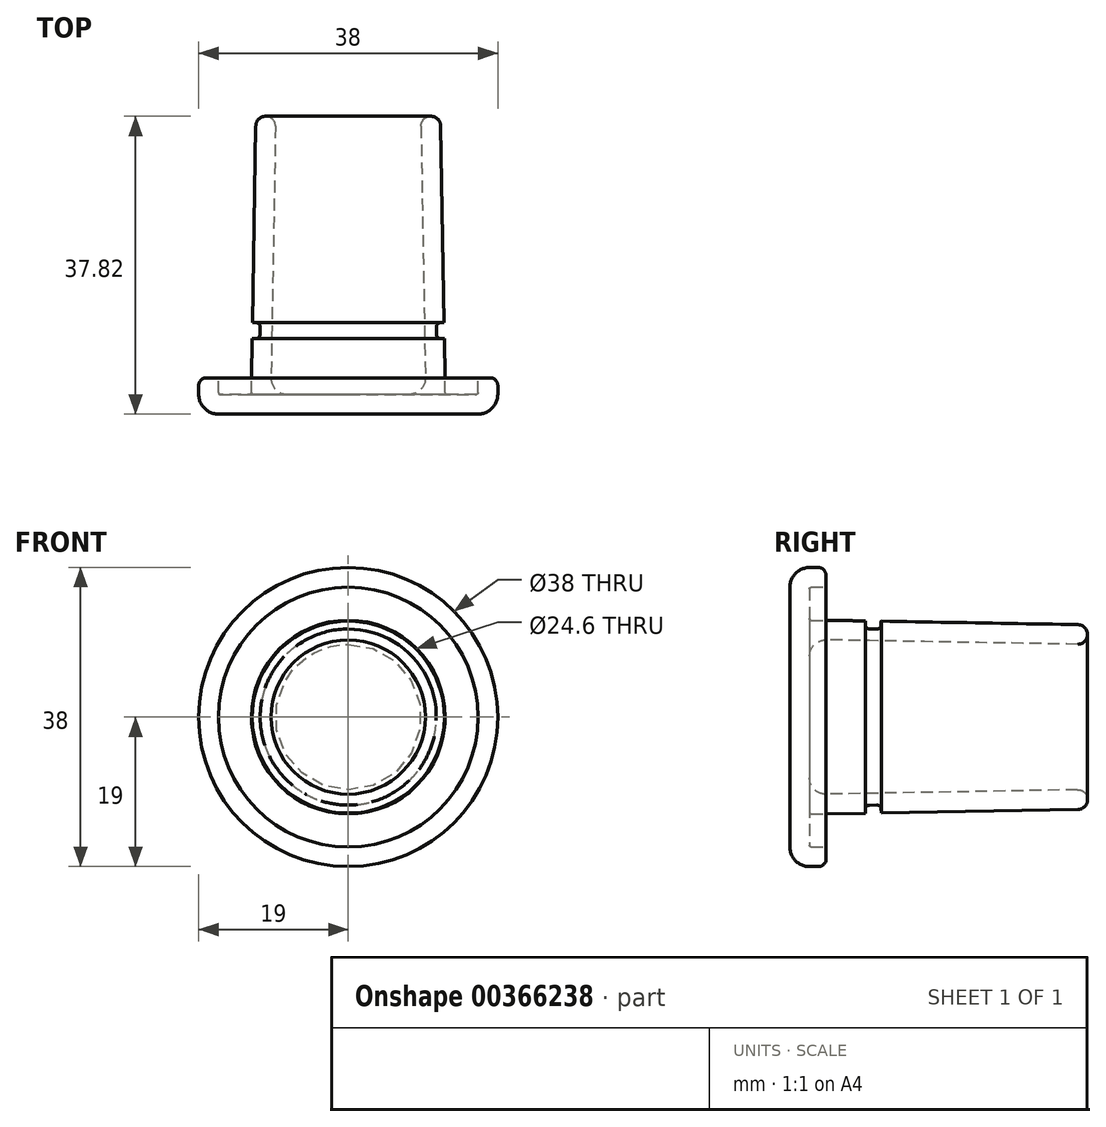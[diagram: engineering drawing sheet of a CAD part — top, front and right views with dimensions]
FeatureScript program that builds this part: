
annotation { "Feature Type Name" : "Feature", "Feature Type Description" : "" }
export const myFeature = defineFeature(function(context is Context, id is Id, definition is map)
    precondition{}
    {
        {
            var Q0;
            Q0=qCreatedBy(makeId("Right.planeOp"),FACE);
            var sketch = newSketch(context, id + "F0", { "sketchPlane" : qUnion([Q0])});
            skLineSegment(sketch, "E0", {"start": v(0, 0) * mm, "end": v(0, 16.5) * mm});
            skLineSegment(sketch, "E1", {"start": v(2.5, 19) * mm, "end": v(3.6, 19) * mm});
            skLineSegment(sketch, "E2", {"start": v(4.6, 18) * mm, "end": v(4.6, 16.7) * mm});
            skLineSegment(sketch, "E3", {"start": v(4.4, 16.5) * mm, "end": v(2.7, 16.5) * mm});
            skLineSegment(sketch, "E4", {"start": v(2.5, 16.3) * mm, "end": v(2.5, 12.5) * mm});
            skLineSegment(sketch, "E5", {"start": v(2.7, 12.3) * mm, "end": v(4.58, 12.3) * mm});
            skLineSegment(sketch, "E6", {"start": v(0, 0) * mm, "end": v(2.5, 0) * mm});
            skArc(sketch, "E7.filletArc", {"start": v(2.5, 19) * mm, "mid": v(0.73, 18.27) * mm, "end": v(0, 16.5) * mm});
            skArc(sketch, "E8.filletArc", {"start": v(4.6, 18) * mm, "mid": v(4.3, 18.7) * mm, "end": v(3.6, 19) * mm});
            skArc(sketch, "E9.filletArc", {"start": v(2.7, 16.5) * mm, "mid": v(2.56, 16.44) * mm, "end": v(2.5, 16.3) * mm});
            skArc(sketch, "E10.filletArc", {"start": v(2.5, 12.5) * mm, "mid": v(2.56, 12.36) * mm, "end": v(2.7, 12.3) * mm});
            skLineSegment(sketch, "E11", {"start": v(2.5, 0) * mm, "end": v(2.5, 7.74) * mm});
            skLineSegment(sketch, "E12", {"start": v(4.56, 9.8) * mm, "end": v(4.56, 9.8) * mm});
            skArc(sketch, "E13.filletArc", {"start": v(4.56, 9.8) * mm, "mid": v(3.1, 9.2) * mm, "end": v(2.5, 7.74) * mm});
            skLineSegment(sketch, "E14", {"start": v(4.58, 12.3) * mm, "end": v(9.6, 12.21) * mm});
            skLineSegment(sketch, "E15", {"start": v(9.6, 12.21) * mm, "end": v(9.6, 11.71) * mm});
            skLineSegment(sketch, "E16", {"start": v(10.08, 11.2) * mm, "end": v(11.08, 11.19) * mm});
            skLineSegment(sketch, "E17", {"start": v(11.6, 11.68) * mm, "end": v(11.6, 12.18) * mm});
            skLineSegment(sketch, "E18", {"start": v(11.6, 12.18) * mm, "end": v(36.6, 11.74) * mm});
            skLineSegment(sketch, "E19", {"start": v(4.56, 9.8) * mm, "end": v(36.55, 9.24) * mm});
            skLineSegment(sketch, "E20", {"start": v(36.6, 11.74) * mm, "end": v(36.55, 9.24) * mm, "construction": true});
            skArc(sketch, "E21", {"start": v(36.6, 11.74) * mm, "mid": v(37.82, 10.47) * mm, "end": v(36.55, 9.24) * mm});
            skPoint(sketch, "E22.visualSharp", {"position": v(9.58, 11.21) * mm});
            skArc(sketch, "E22.filletArc", {"start": v(9.6, 11.71) * mm, "mid": v(9.73, 11.36) * mm, "end": v(10.08, 11.2) * mm});
            skPoint(sketch, "E23.visualSharp", {"position": v(11.58, 11.18) * mm});
            skArc(sketch, "E23.filletArc", {"start": v(11.08, 11.19) * mm, "mid": v(11.44, 11.33) * mm, "end": v(11.6, 11.68) * mm});
            skPoint(sketch, "E24.visualSharp", {"position": v(4.6, 16.5) * mm});
            skArc(sketch, "E24.filletArc", {"start": v(4.4, 16.5) * mm, "mid": v(4.54, 16.56) * mm, "end": v(4.6, 16.7) * mm});
            skLineSegment(sketch, "E25", {"start": v(4.6, 12.3) * mm, "end": v(4.56, 9.8) * mm, "construction": true});
            skLineSegment(sketch, "E26", {"start": v(0, 12.5) * mm, "end": v(2.5, 12.5) * mm, "construction": true});
            skLineSegment(sketch, "E27", {"start": v(3.05, 19) * mm, "end": v(3.05, 16.5) * mm, "construction": true});
            skLineSegment(sketch, "E28", {"start": v(0.86, 18.4) * mm, "end": v(2.5, 16.5) * mm, "construction": true});
            skLineSegment(sketch, "E29", {"start": v(4.56, 7.74) * mm, "end": v(4.56, 9.8) * mm, "construction": true});
            skLineSegment(sketch, "E30", {"start": v(4.56, 7.74) * mm, "end": v(2.5, 7.74) * mm, "construction": true});
            skLineSegment(sketch, "E31", {"start": v(36.57, 10.5) * mm, "end": v(37.82, 10.47) * mm, "construction": true});
            skPoint(sketch, "E32.visualSharp", {"position": v(4.6, 12.3) * mm});
            skSolve(sketch);
        }
        {
            var Q0;
            Q0=sQuery(id+"F0.wireOp",EDGE,"E18");
            var Q1;
            Q1=sQuery(id+"F0.wireOp",EDGE,"E14");
            var Q2;
            Q2=sQuery(id+"F0.wireOp",EDGE,"E0");
            var Q3;
            Q3=sQuery(id+"F0.wireOp",EDGE,"E2");
            var Q4;
            Q4=sQuery(id+"F0.wireOp",EDGE,"E3");
            var Q5;
            Q5=sQuery(id+"F0.wireOp",EDGE,"E4");
            var Q6;
            Q6=sQuery(id+"F0.wireOp",EDGE,"E5");
            var Q7;
            Q7=sQuery(id+"F0.wireOp",EDGE,"E7.filletArc");
            var Q8;
            Q8=sQuery(id+"F0.wireOp",EDGE,"E8.filletArc");
            var Q9;
            Q9=sQuery(id+"F0.wireOp",EDGE,"E11");
            var Q10;
            Q10=sQuery(id+"F0.wireOp",EDGE,"E13.filletArc");
            var Q11;
            Q11=sQuery(id+"F0.wireOp",EDGE,"E21");
            var Q12;
            Q12=sQuery(id+"F0.wireOp",EDGE,"E19");
            var Q13;
            Q13=sQuery(id+"F0.wireOp",EDGE,"E1");
            var Q14;
            Q14=sQuery(id+"F0.wireOp",EDGE,"E16");
            var Q15;
            Q15=sQuery(id+"F0.wireOp",EDGE,"E23.filletArc");
            var Q16;
            Q16=sQuery(id+"F0.wireOp",EDGE,"E17");
            var Q17;
            Q17=sQuery(id+"F0.wireOp",EDGE,"E22.filletArc");
            var Q18;
            Q18=sQuery(id+"F0.wireOp",EDGE,"E15");
            var Q19;
            Q19=sQuery(id+"F0.wireOp",EDGE,"E9.filletArc");
            var Q20;
            Q20=sQuery(id+"F0.wireOp",EDGE,"E10.filletArc");
            var Q21;
            Q21=sQuery(id+"F0.wireOp",EDGE,"E24.filletArc");
            var Q22;
            Q22=sQuery(id+"F0.wireOp",EDGE,"E6");
            revolve(context, id + "F1", {"bodyType" : ToolBodyType.SURFACE, "surfaceEntities" : qUnion([Q0, Q1, Q2, Q3, Q4, Q5, Q6, Q7, Q8, Q9, Q10, Q11, Q12, Q13, Q14, Q15, Q16, Q17, Q18, Q19, Q20, Q21]), "axis" : qUnion([Q22]), "revolveType" : RevolveType.FULL});
        }
    });
